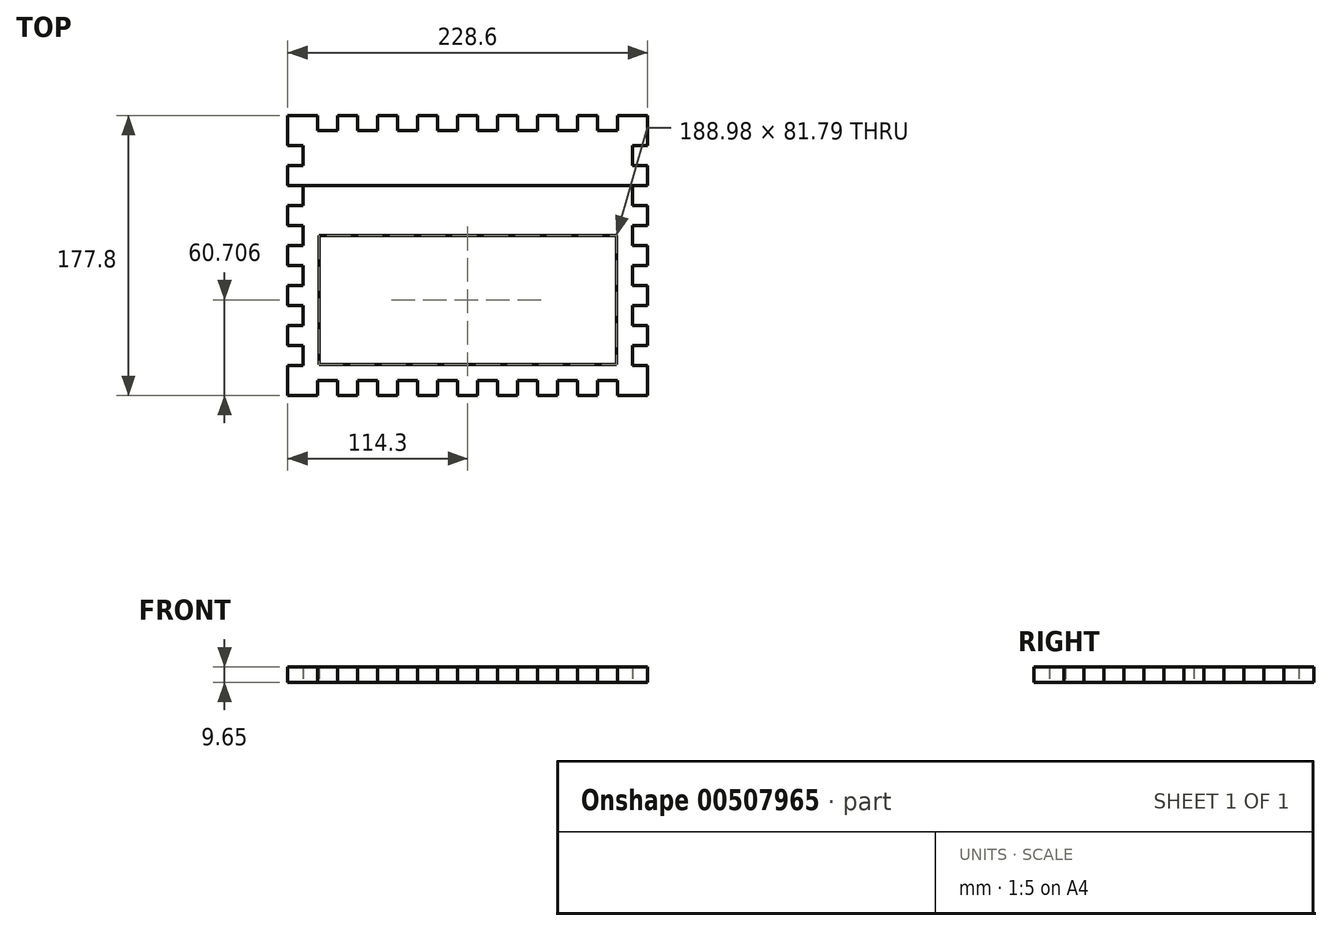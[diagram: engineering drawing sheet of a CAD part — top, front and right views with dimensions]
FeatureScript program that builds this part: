
annotation { "Feature Type Name" : "Feature", "Feature Type Description" : "" }
export const myFeature = defineFeature(function(context is Context, id is Id, definition is map)
    precondition{}
    {
        {
            var Q0;
            Q0=qCreatedBy(makeId("Top.planeOp"),FACE);
            var sketch = newSketch(context, id + "F0", { "sketchPlane" : qUnion([Q0])});
            skLineSegment(sketch, "E0.bottom", {"start": v(0, 0) * mm, "end": v(19.05, 0) * mm});
            skLineSegment(sketch, "E0.left", {"start": v(0, 0) * mm, "end": v(0, -19.05) * mm});
            skLineSegment(sketch, "E1", {"start": v(19.05, 0) * mm, "end": v(19.05, -9.65) * mm});
            skLineSegment(sketch, "E2", {"start": v(19.05, -9.65) * mm, "end": v(31.75, -9.65) * mm});
            skLineSegment(sketch, "E3", {"start": v(31.75, -9.65) * mm, "end": v(31.75, 0) * mm});
            skLineSegment(sketch, "E4", {"start": v(31.75, 0) * mm, "end": v(44.45, 0) * mm});
            skLineSegment(sketch, "E5", {"start": v(44.45, 0) * mm, "end": v(44.45, -9.65) * mm});
            skLineSegment(sketch, "E6", {"start": v(44.45, -9.65) * mm, "end": v(57.15, -9.65) * mm});
            skLineSegment(sketch, "E7", {"start": v(57.15, -9.65) * mm, "end": v(57.15, 0) * mm});
            skLineSegment(sketch, "E8", {"start": v(57.15, 0) * mm, "end": v(69.85, 0) * mm});
            skLineSegment(sketch, "E9", {"start": v(69.85, 0) * mm, "end": v(69.85, -9.65) * mm});
            skLineSegment(sketch, "E10", {"start": v(69.85, -9.65) * mm, "end": v(82.55, -9.65) * mm});
            skLineSegment(sketch, "E11", {"start": v(82.55, -9.65) * mm, "end": v(82.55, 0) * mm});
            skLineSegment(sketch, "E12", {"start": v(82.55, 0) * mm, "end": v(95.25, 0) * mm});
            skLineSegment(sketch, "E13", {"start": v(95.25, 0) * mm, "end": v(95.25, -9.65) * mm});
            skLineSegment(sketch, "E14", {"start": v(95.25, -9.65) * mm, "end": v(107.95, -9.65) * mm});
            skLineSegment(sketch, "E15", {"start": v(107.95, -9.65) * mm, "end": v(107.95, 0) * mm});
            skLineSegment(sketch, "E16.trimOffspring", {"start": v(107.95, 0) * mm, "end": v(120.65, 0) * mm});
            skLineSegment(sketch, "E17", {"start": v(120.65, 0) * mm, "end": v(120.65, -9.65) * mm});
            skLineSegment(sketch, "E18", {"start": v(120.65, -9.65) * mm, "end": v(133.35, -9.65) * mm});
            skLineSegment(sketch, "E19", {"start": v(133.35, -9.65) * mm, "end": v(133.35, 0) * mm});
            skLineSegment(sketch, "E20", {"start": v(133.35, 0) * mm, "end": v(146.05, 0) * mm});
            skLineSegment(sketch, "E21", {"start": v(146.05, 0) * mm, "end": v(146.05, -9.65) * mm});
            skLineSegment(sketch, "E22", {"start": v(146.05, -9.65) * mm, "end": v(158.75, -9.65) * mm});
            skLineSegment(sketch, "E23", {"start": v(158.75, -9.65) * mm, "end": v(158.75, 0) * mm});
            skLineSegment(sketch, "E24", {"start": v(158.75, 0) * mm, "end": v(171.45, 0) * mm});
            skLineSegment(sketch, "E25", {"start": v(171.45, 0) * mm, "end": v(171.45, -9.65) * mm});
            skLineSegment(sketch, "E26", {"start": v(171.45, -9.65) * mm, "end": v(184.15, -9.65) * mm});
            skLineSegment(sketch, "E27", {"start": v(184.15, -9.65) * mm, "end": v(184.15, 0) * mm});
            skLineSegment(sketch, "E28.trimOffspring", {"start": v(184.15, 0) * mm, "end": v(196.85, 0) * mm});
            skLineSegment(sketch, "E29", {"start": v(196.85, 0) * mm, "end": v(196.85, -9.65) * mm});
            skLineSegment(sketch, "E30", {"start": v(196.85, -9.65) * mm, "end": v(209.55, -9.65) * mm});
            skLineSegment(sketch, "E31", {"start": v(209.55, -9.65) * mm, "end": v(209.55, 0) * mm});
            skLineSegment(sketch, "E32.trimOffspring", {"start": v(209.55, 0) * mm, "end": v(228.6, 0) * mm});
            skLineSegment(sketch, "E33", {"start": v(0, -19.05) * mm, "end": v(9.65, -19.05) * mm});
            skLineSegment(sketch, "E34", {"start": v(9.65, -19.05) * mm, "end": v(9.65, -31.75) * mm});
            skLineSegment(sketch, "E35", {"start": v(9.65, -31.75) * mm, "end": v(0, -31.75) * mm});
            skLineSegment(sketch, "E36", {"start": v(0, -31.75) * mm, "end": v(0, -44.45) * mm});
            skLineSegment(sketch, "E37", {"start": v(0, -44.45) * mm, "end": v(9.65, -44.45) * mm});
            skLineSegment(sketch, "E38", {"start": v(9.65, -44.45) * mm, "end": v(9.65, -57.15) * mm});
            skLineSegment(sketch, "E39", {"start": v(9.65, -57.15) * mm, "end": v(0, -57.15) * mm});
            skLineSegment(sketch, "E40.trimOffspring", {"start": v(0, -57.15) * mm, "end": v(0, -69.85) * mm});
            skLineSegment(sketch, "E41", {"start": v(0, -69.85) * mm, "end": v(9.65, -69.85) * mm});
            skLineSegment(sketch, "E42", {"start": v(9.65, -69.85) * mm, "end": v(9.65, -82.55) * mm});
            skLineSegment(sketch, "E43", {"start": v(9.65, -82.55) * mm, "end": v(0, -82.55) * mm});
            skLineSegment(sketch, "E44", {"start": v(0, -82.55) * mm, "end": v(0, -95.25) * mm});
            skLineSegment(sketch, "E45", {"start": v(0, -95.25) * mm, "end": v(9.65, -95.25) * mm});
            skLineSegment(sketch, "E46", {"start": v(9.65, -95.25) * mm, "end": v(9.65, -107.95) * mm});
            skLineSegment(sketch, "E47", {"start": v(9.65, -107.95) * mm, "end": v(0, -107.95) * mm});
            skLineSegment(sketch, "E48", {"start": v(0, -107.95) * mm, "end": v(0, -120.65) * mm});
            skLineSegment(sketch, "E49", {"start": v(0, -120.65) * mm, "end": v(9.65, -120.65) * mm});
            skLineSegment(sketch, "E50", {"start": v(9.65, -120.65) * mm, "end": v(9.65, -133.35) * mm});
            skLineSegment(sketch, "E51", {"start": v(9.65, -133.35) * mm, "end": v(0, -133.35) * mm});
            skLineSegment(sketch, "E52.trimOffspring", {"start": v(0, -133.35) * mm, "end": v(0, -146.05) * mm});
            skLineSegment(sketch, "E53", {"start": v(0, -146.05) * mm, "end": v(9.65, -146.05) * mm});
            skLineSegment(sketch, "E54", {"start": v(9.65, -146.05) * mm, "end": v(9.65, -158.75) * mm});
            skLineSegment(sketch, "E55", {"start": v(9.65, -158.75) * mm, "end": v(0, -158.75) * mm});
            skLineSegment(sketch, "E56.trimOffspring", {"start": v(0, -158.75) * mm, "end": v(0, -177.8) * mm});
            skLineSegment(sketch, "E57", {"start": v(114.3, 0) * mm, "end": v(114.3, -53.86) * mm, "construction": true});
            skLineSegment(sketch, "E58.MirrorCS", {"start": v(228.6, 0) * mm, "end": v(228.6, -19.05) * mm});
            skLineSegment(sketch, "E59.MirrorCS", {"start": v(228.6, -19.05) * mm, "end": v(218.95, -19.05) * mm});
            skLineSegment(sketch, "E60.MirrorCS", {"start": v(218.95, -19.05) * mm, "end": v(218.95, -31.75) * mm});
            skLineSegment(sketch, "E61.MirrorCS", {"start": v(218.95, -31.75) * mm, "end": v(228.6, -31.75) * mm});
            skLineSegment(sketch, "E62.MirrorCS", {"start": v(228.6, -31.75) * mm, "end": v(228.6, -44.45) * mm});
            skLineSegment(sketch, "E63.MirrorCS", {"start": v(228.6, -44.45) * mm, "end": v(218.95, -44.45) * mm});
            skLineSegment(sketch, "E64.MirrorCS", {"start": v(218.95, -44.45) * mm, "end": v(218.95, -57.15) * mm});
            skLineSegment(sketch, "E65.MirrorCS", {"start": v(218.95, -57.15) * mm, "end": v(228.6, -57.15) * mm});
            skLineSegment(sketch, "E66.MirrorCS", {"start": v(228.6, -57.15) * mm, "end": v(228.6, -69.85) * mm});
            skLineSegment(sketch, "E67.MirrorCS", {"start": v(228.6, -69.85) * mm, "end": v(218.95, -69.85) * mm});
            skLineSegment(sketch, "E68.MirrorCS", {"start": v(218.95, -69.85) * mm, "end": v(218.95, -82.55) * mm});
            skLineSegment(sketch, "E69.MirrorCS", {"start": v(218.95, -82.55) * mm, "end": v(228.6, -82.55) * mm});
            skLineSegment(sketch, "E70.MirrorCS", {"start": v(228.6, -82.55) * mm, "end": v(228.6, -95.25) * mm});
            skLineSegment(sketch, "E71.MirrorCS", {"start": v(228.6, -95.25) * mm, "end": v(218.95, -95.25) * mm});
            skLineSegment(sketch, "E72.MirrorCS", {"start": v(218.95, -95.25) * mm, "end": v(218.95, -107.95) * mm});
            skLineSegment(sketch, "E73.MirrorCS", {"start": v(218.95, -107.95) * mm, "end": v(228.6, -107.95) * mm});
            skLineSegment(sketch, "E74.MirrorCS", {"start": v(228.6, -107.95) * mm, "end": v(228.6, -120.65) * mm});
            skLineSegment(sketch, "E75.MirrorCS", {"start": v(228.6, -120.65) * mm, "end": v(218.95, -120.65) * mm});
            skLineSegment(sketch, "E76.MirrorCS", {"start": v(218.95, -120.65) * mm, "end": v(218.95, -133.35) * mm});
            skLineSegment(sketch, "E77.MirrorCS", {"start": v(218.95, -133.35) * mm, "end": v(228.6, -133.35) * mm});
            skLineSegment(sketch, "E78.MirrorCS", {"start": v(228.6, -133.35) * mm, "end": v(228.6, -146.05) * mm});
            skLineSegment(sketch, "E79.MirrorCS", {"start": v(228.6, -146.05) * mm, "end": v(218.95, -146.05) * mm});
            skLineSegment(sketch, "E80.MirrorCS", {"start": v(218.95, -146.05) * mm, "end": v(218.95, -158.75) * mm});
            skLineSegment(sketch, "E81.MirrorCS", {"start": v(218.95, -158.75) * mm, "end": v(228.6, -158.75) * mm});
            skLineSegment(sketch, "E82.MirrorCS", {"start": v(228.6, -158.75) * mm, "end": v(228.6, -177.8) * mm});
            skLineSegment(sketch, "E83", {"start": v(0, -88.9) * mm, "end": v(56.96, -88.9) * mm, "construction": true});
            skLineSegment(sketch, "E84.MirrorCS", {"start": v(0, -177.8) * mm, "end": v(19.05, -177.8) * mm});
            skLineSegment(sketch, "E85.MirrorCS", {"start": v(19.05, -177.8) * mm, "end": v(19.05, -168.15) * mm});
            skLineSegment(sketch, "E86.MirrorCS", {"start": v(19.05, -168.15) * mm, "end": v(31.75, -168.15) * mm});
            skLineSegment(sketch, "E87.MirrorCS", {"start": v(31.75, -168.15) * mm, "end": v(31.75, -177.8) * mm});
            skLineSegment(sketch, "E88.MirrorCS", {"start": v(31.75, -177.8) * mm, "end": v(44.45, -177.8) * mm});
            skLineSegment(sketch, "E89.MirrorCS", {"start": v(44.45, -177.8) * mm, "end": v(44.45, -168.15) * mm});
            skLineSegment(sketch, "E90.MirrorCS", {"start": v(44.45, -168.15) * mm, "end": v(57.15, -168.15) * mm});
            skLineSegment(sketch, "E91.MirrorCS", {"start": v(57.15, -168.15) * mm, "end": v(57.15, -177.8) * mm});
            skLineSegment(sketch, "E92.MirrorCS", {"start": v(57.15, -177.8) * mm, "end": v(69.85, -177.8) * mm});
            skLineSegment(sketch, "E93.MirrorCS", {"start": v(69.85, -177.8) * mm, "end": v(69.85, -168.15) * mm});
            skLineSegment(sketch, "E94.MirrorCS", {"start": v(69.85, -168.15) * mm, "end": v(82.55, -168.15) * mm});
            skLineSegment(sketch, "E95.MirrorCS", {"start": v(82.55, -168.15) * mm, "end": v(82.55, -177.8) * mm});
            skLineSegment(sketch, "E96.MirrorCS", {"start": v(82.55, -177.8) * mm, "end": v(95.25, -177.8) * mm});
            skLineSegment(sketch, "E97.MirrorCS", {"start": v(95.25, -177.8) * mm, "end": v(95.25, -168.15) * mm});
            skLineSegment(sketch, "E98.MirrorCS", {"start": v(95.25, -168.15) * mm, "end": v(107.95, -168.15) * mm});
            skLineSegment(sketch, "E99.MirrorCS", {"start": v(107.95, -168.15) * mm, "end": v(107.95, -177.8) * mm});
            skLineSegment(sketch, "E100.MirrorCS", {"start": v(107.95, -177.8) * mm, "end": v(120.65, -177.8) * mm});
            skLineSegment(sketch, "E101.MirrorCS", {"start": v(120.65, -177.8) * mm, "end": v(120.65, -168.15) * mm});
            skLineSegment(sketch, "E102.MirrorCS", {"start": v(120.65, -168.15) * mm, "end": v(133.35, -168.15) * mm});
            skLineSegment(sketch, "E103.MirrorCS", {"start": v(133.35, -168.15) * mm, "end": v(133.35, -177.8) * mm});
            skLineSegment(sketch, "E104.MirrorCS", {"start": v(133.35, -177.8) * mm, "end": v(146.05, -177.8) * mm});
            skLineSegment(sketch, "E105.MirrorCS", {"start": v(146.05, -177.8) * mm, "end": v(146.05, -168.15) * mm});
            skLineSegment(sketch, "E106.MirrorCS", {"start": v(146.05, -168.15) * mm, "end": v(158.75, -168.15) * mm});
            skLineSegment(sketch, "E107.MirrorCS", {"start": v(158.75, -168.15) * mm, "end": v(158.75, -177.8) * mm});
            skLineSegment(sketch, "E108.MirrorCS", {"start": v(158.75, -177.8) * mm, "end": v(171.45, -177.8) * mm});
            skLineSegment(sketch, "E109.MirrorCS", {"start": v(171.45, -177.8) * mm, "end": v(171.45, -168.15) * mm});
            skLineSegment(sketch, "E110.MirrorCS", {"start": v(171.45, -168.15) * mm, "end": v(184.15, -168.15) * mm});
            skLineSegment(sketch, "E111.MirrorCS", {"start": v(184.15, -168.15) * mm, "end": v(184.15, -177.8) * mm});
            skLineSegment(sketch, "E112.MirrorCS", {"start": v(184.15, -177.8) * mm, "end": v(196.85, -177.8) * mm});
            skLineSegment(sketch, "E113.MirrorCS", {"start": v(196.85, -177.8) * mm, "end": v(196.85, -168.15) * mm});
            skLineSegment(sketch, "E114.MirrorCS", {"start": v(196.85, -168.15) * mm, "end": v(209.55, -168.15) * mm});
            skLineSegment(sketch, "E115.MirrorCS", {"start": v(209.55, -168.15) * mm, "end": v(209.55, -177.8) * mm});
            skLineSegment(sketch, "E116.MirrorCS", {"start": v(209.55, -177.8) * mm, "end": v(228.6, -177.8) * mm});
            skLineSegment(sketch, "E117.bottom", {"start": v(19.81, -76.2) * mm, "end": v(208.79, -76.2) * mm});
            skLineSegment(sketch, "E117.top", {"start": v(19.81, -157.99) * mm, "end": v(208.79, -157.99) * mm});
            skLineSegment(sketch, "E117.left", {"start": v(19.81, -76.2) * mm, "end": v(19.81, -157.99) * mm});
            skLineSegment(sketch, "E117.right", {"start": v(208.79, -76.2) * mm, "end": v(208.79, -157.99) * mm});
            skLineSegment(sketch, "E118", {"start": v(9.65, -44.45) * mm, "end": v(218.95, -44.45) * mm});
            skSolve(sketch);
        }
        {
            var Q0;
            Q0=makeQuery(id+"F0.imprint","IMPRINT",FACE,{"disambiguationData":[TD([[makeQuery(id+"F0.imprint","IMPRINT",EDGE,{"derivedFrom":sQuery(id+"F0.wireOp",EDGE,"E0.bottom")}),-1.0]])]});
            extrude(context, id + "F1", {"entities" : qUnion([Q0]), "depth" : 9.65 * mm});
        }
        {
            var Q0;
            Q0=makeQuery(id+"F0.imprint","IMPRINT",FACE,{"disambiguationData":[TD([[makeQuery(id+"F0.imprint","IMPRINT",EDGE,{"derivedFrom":sQuery(id+"F0.wireOp",EDGE,"E39")}),1.0]])]});
            extrude(context, id + "F2", {"entities" : qUnion([Q0]), "depth" : 9.65 * mm});
        }
    });
